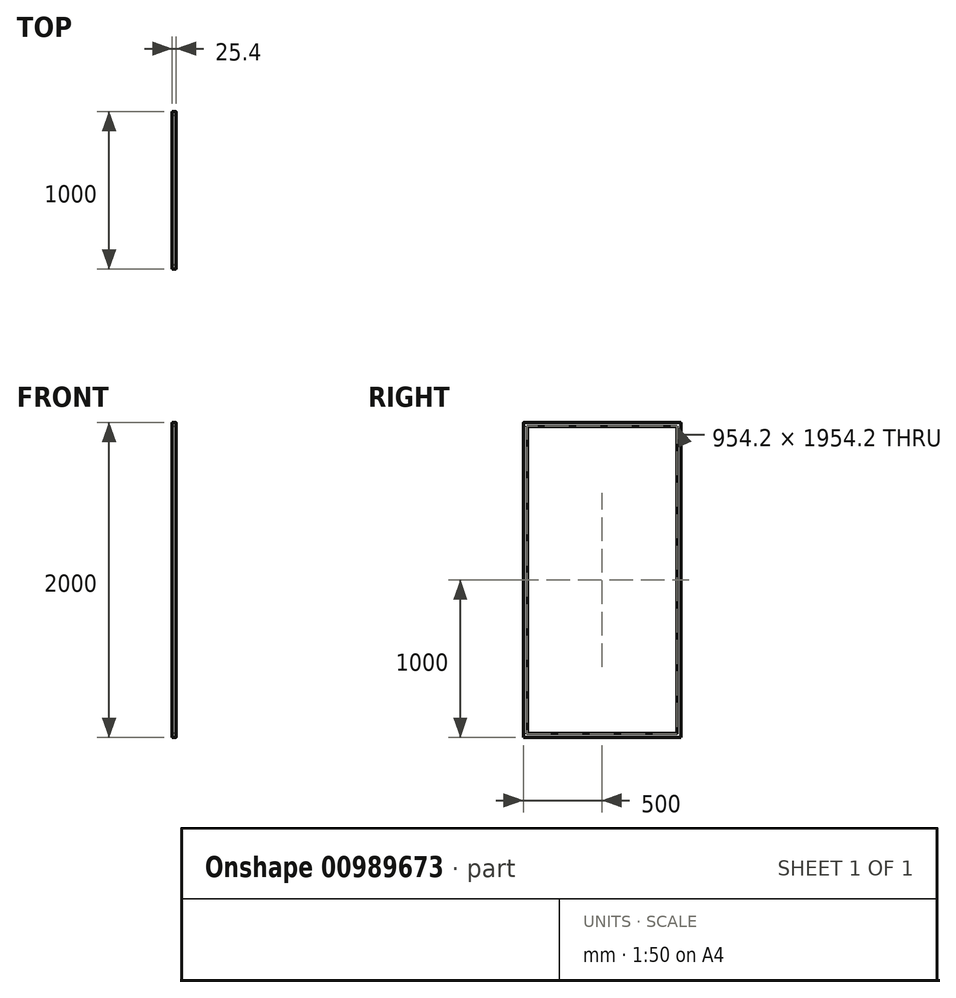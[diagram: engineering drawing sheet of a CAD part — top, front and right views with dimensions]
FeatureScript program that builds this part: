
annotation { "Feature Type Name" : "Feature", "Feature Type Description" : "" }
export const myFeature = defineFeature(function(context is Context, id is Id, definition is map)
    precondition{}
    {
        {
            var Q0;
            Q0=qCreatedBy(makeId("Right.planeOp"),FACE);
            var sketch = newSketch(context, id + "F0", { "sketchPlane" : qUnion([Q0])});
            skLineSegment(sketch, "E0.bottom", {"start": v(500, 1000) * mm, "end": v(-500, 1000) * mm});
            skLineSegment(sketch, "E0.top", {"start": v(500, -1000) * mm, "end": v(-500, -1000) * mm});
            skLineSegment(sketch, "E0.left", {"start": v(500, 1000) * mm, "end": v(500, -1000) * mm});
            skLineSegment(sketch, "E0.right", {"start": v(-500, 1000) * mm, "end": v(-500, -1000) * mm});
            skPoint(sketch, "E0.middle", {"position": v(0, 0) * mm});
            skLineSegment(sketch, "E1.0", {"start": v(474.6, 974.6) * mm, "end": v(-474.6, 974.6) * mm});
            skLineSegment(sketch, "E1.1", {"start": v(474.6, 974.6) * mm, "end": v(474.6, -974.6) * mm});
            skLineSegment(sketch, "E1.2", {"start": v(474.6, -974.6) * mm, "end": v(-474.6, -974.6) * mm});
            skLineSegment(sketch, "E1.3", {"start": v(-474.6, 974.6) * mm, "end": v(-474.6, -974.6) * mm});
            skSolve(sketch);
        }
        {
            var Q0;
            Q0=makeQuery(id+"F0.imprint","IMPRINT",FACE,{"disambiguationData":[TD([[makeQuery(id+"F0.imprint","IMPRINT",EDGE,{"derivedFrom":sQuery(id+"F0.wireOp",EDGE,"E0.bottom")}),1.0]])]});
            extrude(context, id + "F1", {"entities" : qUnion([Q0]), "depth" : 25.4 * mm, "offsetDistance" : 25 * mm});
        }
        {
            var Q0;
            Q0=makeQuery(id+"F1.opExtrude","CAP_EDGE",EDGE,{"disambiguationData":[OSD([sQuery(id+"F0.wireOp",EDGE,"E0.bottom")])],"isStart":false});
            var Q1;
            Q1=makeQuery(id+"F1.opExtrude","CAP_EDGE",EDGE,{"disambiguationData":[OSD([sQuery(id+"F0.wireOp",EDGE,"E1.0")])],"isStart":false});
            var Q2;
            Q2=makeQuery(id+"F1.opExtrude","CAP_EDGE",EDGE,{"disambiguationData":[OSD([sQuery(id+"F0.wireOp",EDGE,"E0.bottom")])],"isStart":true});
            var Q3;
            Q3=makeQuery(id+"F1.opExtrude","CAP_EDGE",EDGE,{"disambiguationData":[OSD([sQuery(id+"F0.wireOp",EDGE,"E1.0")])],"isStart":true});
            var Q4;
            Q4=makeQuery(id+"F1.opExtrude","CAP_EDGE",EDGE,{"disambiguationData":[OSD([sQuery(id+"F0.wireOp",EDGE,"E0.right")])],"isStart":true});
            var Q5;
            Q5=makeQuery(id+"F1.opExtrude","CAP_EDGE",EDGE,{"disambiguationData":[OSD([sQuery(id+"F0.wireOp",EDGE,"E0.right")])],"isStart":false});
            var Q6;
            Q6=makeQuery(id+"F1.opExtrude","CAP_EDGE",EDGE,{"disambiguationData":[OSD([sQuery(id+"F0.wireOp",EDGE,"E1.3")])],"isStart":true});
            var Q7;
            Q7=makeQuery(id+"F1.opExtrude","CAP_EDGE",EDGE,{"disambiguationData":[OSD([sQuery(id+"F0.wireOp",EDGE,"E1.3")])],"isStart":false});
            var Q8;
            Q8=makeQuery(id+"F1.opExtrude","CAP_EDGE",EDGE,{"disambiguationData":[OSD([sQuery(id+"F0.wireOp",EDGE,"E0.left")])],"isStart":false});
            var Q9;
            Q9=makeQuery(id+"F1.opExtrude","CAP_EDGE",EDGE,{"disambiguationData":[OSD([sQuery(id+"F0.wireOp",EDGE,"E0.left")])],"isStart":true});
            var Q10;
            Q10=makeQuery(id+"F1.opExtrude","CAP_EDGE",EDGE,{"disambiguationData":[OSD([sQuery(id+"F0.wireOp",EDGE,"E1.1")])],"isStart":false});
            var Q11;
            Q11=makeQuery(id+"F1.opExtrude","CAP_EDGE",EDGE,{"disambiguationData":[OSD([sQuery(id+"F0.wireOp",EDGE,"E1.2")])],"isStart":false});
            var Q12;
            Q12=makeQuery(id+"F1.opExtrude","CAP_EDGE",EDGE,{"disambiguationData":[OSD([sQuery(id+"F0.wireOp",EDGE,"E0.top")])],"isStart":false});
            var Q13;
            Q13=makeQuery(id+"F1.opExtrude","CAP_EDGE",EDGE,{"disambiguationData":[OSD([sQuery(id+"F0.wireOp",EDGE,"E0.top")])],"isStart":true});
            var Q14;
            Q14=makeQuery(id+"F1.opExtrude","CAP_EDGE",EDGE,{"disambiguationData":[OSD([sQuery(id+"F0.wireOp",EDGE,"E1.1")])],"isStart":true});
            var Q15;
            Q15=makeQuery(id+"F1.opExtrude","CAP_EDGE",EDGE,{"disambiguationData":[OSD([sQuery(id+"F0.wireOp",EDGE,"E1.2")])],"isStart":true});
            fillet(context, id + "F2", {"entities" : qUnion([Q0, Q1, Q2, Q3, Q4, Q5, Q6, Q7, Q8, Q9, Q10, Q11, Q12, Q13, Q14, Q15]), "radius" : 2.5 * mm, "tangentPropagation" : true, "allowEdgeOverflow" : false});
        }
    });
